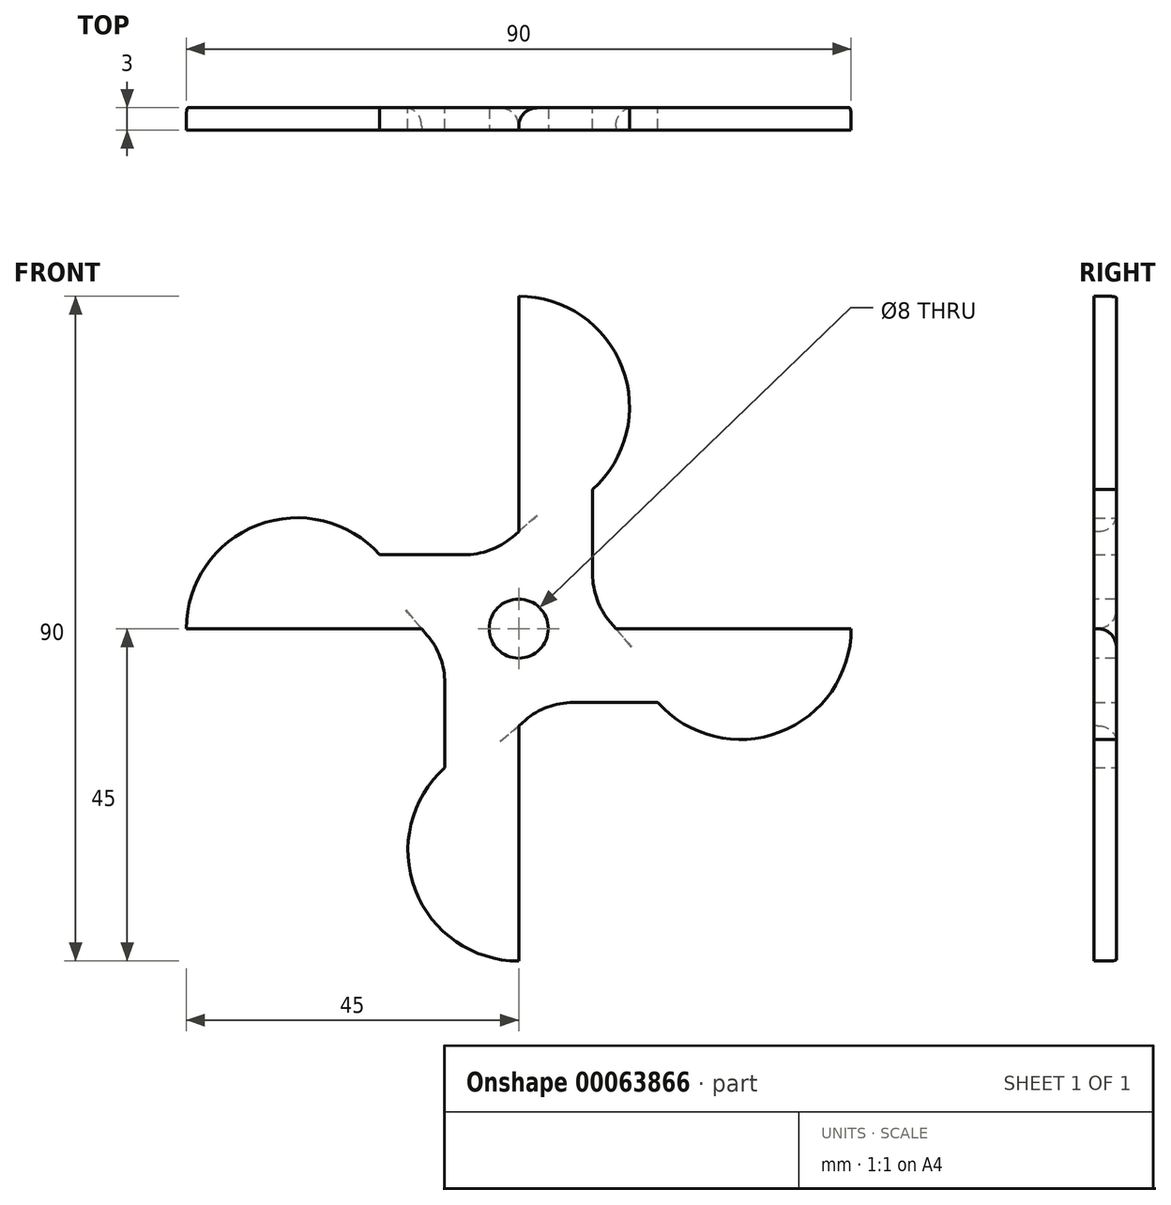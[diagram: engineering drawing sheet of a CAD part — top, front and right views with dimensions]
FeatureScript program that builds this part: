
annotation { "Feature Type Name" : "Feature", "Feature Type Description" : "" }
export const myFeature = defineFeature(function(context is Context, id is Id, definition is map)
    precondition{}
    {
        {
            var Q0;
            Q0=qCreatedBy(makeId("Front.planeOp"),FACE);
            var sketch = newSketch(context, id + "F0", { "sketchPlane" : qUnion([Q0])});
            skArc(sketch, "E0", {"start": v(10, 18.82) * mm, "mid": v(14.01, 35.35) * mm, "end": v(0, 45) * mm});
            skArc(sketch, "E1", {"start": v(10, 21.7) * mm, "mid": v(11.77, 35.52) * mm, "end": v(0, 43) * mm});
            skLineSegment(sketch, "E2", {"start": v(0, 13.15) * mm, "end": v(0, 10) * mm});
            skLineSegment(sketch, "E3", {"start": v(10, 7.38) * mm, "end": v(10, 18.82) * mm});
            skLineSegment(sketch, "E4", {"start": v(0, 43) * mm, "end": v(0, 45) * mm});
            skArc(sketch, "E5.1.1", {"start": v(-21.7, 10) * mm, "mid": v(-35.52, 11.77) * mm, "end": v(-43, 0) * mm});
            skLineSegment(sketch, "E5.1.2", {"start": v(-43, 0) * mm, "end": v(-45, 0) * mm});
            skArc(sketch, "E5.1.3", {"start": v(-18.82, 10) * mm, "mid": v(-35.35, 14.01) * mm, "end": v(-45, 0) * mm});
            skLineSegment(sketch, "E5.1.4", {"start": v(-7.38, 10) * mm, "end": v(-18.82, 10) * mm});
            skArc(sketch, "E5.2.1", {"start": v(-10, -21.7) * mm, "mid": v(-11.77, -35.52) * mm, "end": v(0, -43) * mm});
            skLineSegment(sketch, "E5.2.2", {"start": v(0, -43) * mm, "end": v(0, -45) * mm});
            skArc(sketch, "E5.2.3", {"start": v(-10, -18.82) * mm, "mid": v(-14.01, -35.35) * mm, "end": v(0, -45) * mm});
            skLineSegment(sketch, "E5.2.4", {"start": v(-10, -7.38) * mm, "end": v(-10, -18.82) * mm});
            skLineSegment(sketch, "E5.3.0", {"start": v(17, 0) * mm, "end": v(17, 0) * mm});
            skArc(sketch, "E5.3.1", {"start": v(21.7, -10) * mm, "mid": v(35.52, -11.77) * mm, "end": v(43, 0) * mm});
            skLineSegment(sketch, "E5.3.2", {"start": v(43, 0) * mm, "end": v(45, 0) * mm});
            skArc(sketch, "E5.3.3", {"start": v(18.82, -10) * mm, "mid": v(35.35, -14.01) * mm, "end": v(45, 0) * mm});
            skLineSegment(sketch, "E5.3.4", {"start": v(7.38, -10) * mm, "end": v(18.82, -10) * mm});
            skPoint(sketch, "E5.center", {"position": v(0, 0) * mm});
            skPoint(sketch, "E6.visualSharp", {"position": v(10, 0) * mm});
            skLineSegment(sketch, "E7", {"start": v(10, 21.7) * mm, "end": v(-0.88, 12.4) * mm});
            skPoint(sketch, "E8.orphan", {"position": v(0, 17) * mm});
            skPoint(sketch, "E9.newPointB", {"position": v(0, 10) * mm});
            skArc(sketch, "E9.filletArc", {"start": v(-7.38, 10) * mm, "mid": v(-3.92, 10.62) * mm, "end": v(-0.88, 12.4) * mm});
            skArc(sketch, "E10.1.0", {"start": v(-10, -7.38) * mm, "mid": v(-10.62, -3.92) * mm, "end": v(-12.4, -0.88) * mm});
            skLineSegment(sketch, "E10.1.1", {"start": v(-21.7, 10) * mm, "end": v(-12.4, -0.88) * mm});
            skArc(sketch, "E10.2.0", {"start": v(7.38, -10) * mm, "mid": v(3.92, -10.62) * mm, "end": v(0.88, -12.4) * mm});
            skLineSegment(sketch, "E10.2.1", {"start": v(-10, -21.7) * mm, "end": v(0.88, -12.4) * mm});
            skArc(sketch, "E10.3.0", {"start": v(10, 7.38) * mm, "mid": v(10.62, 3.92) * mm, "end": v(12.4, 0.88) * mm});
            skLineSegment(sketch, "E10.3.1", {"start": v(21.7, -10) * mm, "end": v(12.4, 0.88) * mm});
            skPoint(sketch, "E11.orphan", {"position": v(17, 0) * mm});
            skPoint(sketch, "E12.orphan", {"position": v(10, 7) * mm});
            skPoint(sketch, "E13.orphan", {"position": v(0, -17) * mm});
            skPoint(sketch, "E14.orphan", {"position": v(0, -10) * mm});
            skPoint(sketch, "E15.orphan", {"position": v(-10, 0) * mm});
            skPoint(sketch, "E16.orphan", {"position": v(-17, 0) * mm});
            skCircle(sketch, "E17", {"center": v(0, 0) * mm, "radius": 3.75 * mm});
            skSolve(sketch);
        }
        {
            var Q0;
            Q0=makeQuery(id+"F0.imprint","IMPRINT",FACE,{"disambiguationData":[TD([[makeQuery(id+"F0.imprint","IMPRINT",EDGE,{"derivedFrom":sQuery(id+"F0.wireOp",EDGE,"E0")}),1.0]])]});
            extrude(context, id + "F1", {"entities" : qUnion([Q0]), "depth" : 5 * mm});
        }
        {
            var Q0;
            Q0=makeQuery(id+"F1.opExtrude","CAP_FACE",FACE,{"disambiguationData":[OSD([sQuery(id+"F0.wireOp",EDGE,"E0"),sQuery(id+"F0.wireOp",EDGE,"E1"),sQuery(id+"F0.wireOp",EDGE,"E3"),sQuery(id+"F0.wireOp",EDGE,"E4"),sQuery(id+"F0.wireOp",EDGE,"E5.1.1"),sQuery(id+"F0.wireOp",EDGE,"E5.1.2"),sQuery(id+"F0.wireOp",EDGE,"E5.1.3"),sQuery(id+"F0.wireOp",EDGE,"E5.1.4"),sQuery(id+"F0.wireOp",EDGE,"E5.2.1"),sQuery(id+"F0.wireOp",EDGE,"E5.2.2"),sQuery(id+"F0.wireOp",EDGE,"E5.2.3"),sQuery(id+"F0.wireOp",EDGE,"E5.2.4"),sQuery(id+"F0.wireOp",EDGE,"E5.3.1"),sQuery(id+"F0.wireOp",EDGE,"E5.3.2"),sQuery(id+"F0.wireOp",EDGE,"E5.3.3"),sQuery(id+"F0.wireOp",EDGE,"E5.3.4"),sQuery(id+"F0.wireOp",EDGE,"E7"),sQuery(id+"F0.wireOp",EDGE,"E9.filletArc"),sQuery(id+"F0.wireOp",EDGE,"E10.1.0"),sQuery(id+"F0.wireOp",EDGE,"E10.1.1"),sQuery(id+"F0.wireOp",EDGE,"E10.2.0"),sQuery(id+"F0.wireOp",EDGE,"E10.2.1"),sQuery(id+"F0.wireOp",EDGE,"E10.3.0"),sQuery(id+"F0.wireOp",EDGE,"E10.3.1"),sQuery(id+"F0.wireOp",EDGE,"E17")])],"isStart":true});
            var sketch = newSketch(context, id + "F2", { "sketchPlane" : qUnion([Q0])});
            skArc(sketch, "E18", {"start": v(0, 45) * mm, "mid": v(-14.01, 35.35) * mm, "end": v(-10, 18.82) * mm});
            skPoint(sketch, "E18.first.point", {"position": v(-2.98, 44.7) * mm});
            skPoint(sketch, "E18.second.point", {"position": v(-12.28, 38.61) * mm});
            skPoint(sketch, "E18.third.point", {"position": v(-10.97, 19.77) * mm});
            skLineSegment(sketch, "E19", {"start": v(0, 9.88) * mm, "end": v(0, 45) * mm});
            skLineSegment(sketch, "E20", {"start": v(-10, 18.82) * mm, "end": v(-10, 7.38) * mm});
            skArc(sketch, "E21", {"start": v(-12.4, 0.88) * mm, "mid": v(-10.62, 3.92) * mm, "end": v(-10, 7.38) * mm});
            skPoint(sketch, "E21.first.point", {"position": v(-11.49, 2.13) * mm});
            skPoint(sketch, "E21.second.point", {"position": v(-11, 3.02) * mm});
            skPoint(sketch, "E21.third.point", {"position": v(-10.2, 5.4) * mm});
            skLineSegment(sketch, "E22", {"start": v(-13.15, 0) * mm, "end": v(-12.4, 0.88) * mm});
            skLineSegment(sketch, "E23", {"start": v(-13.15, 0) * mm, "end": v(-3.75, 0) * mm});
            skLineSegment(sketch, "E24", {"start": v(0, 3.75) * mm, "end": v(0, 9.88) * mm});
            skArc(sketch, "E25", {"start": v(0, 3.75) * mm, "mid": v(-2.65, 2.65) * mm, "end": v(-3.75, 0) * mm});
            skPoint(sketch, "E25.third.point", {"position": v(-2.3, 2.96) * mm});
            skArc(sketch, "E26.1.0", {"start": v(-3.75, 0) * mm, "mid": v(-2.65, -2.65) * mm, "end": v(0, -3.75) * mm});
            skLineSegment(sketch, "E26.1.1", {"start": v(0, -13.15) * mm, "end": v(-0.88, -12.4) * mm});
            skArc(sketch, "E26.1.2", {"start": v(-0.88, -12.4) * mm, "mid": v(-3.92, -10.62) * mm, "end": v(-7.38, -10) * mm});
            skLineSegment(sketch, "E26.1.3", {"start": v(-18.82, -10) * mm, "end": v(-7.38, -10) * mm});
            skArc(sketch, "E26.1.4", {"start": v(-45, 0) * mm, "mid": v(-35.35, -14.01) * mm, "end": v(-18.82, -10) * mm});
            skLineSegment(sketch, "E26.1.5", {"start": v(-9.88, 0) * mm, "end": v(-45, 0) * mm});
            skLineSegment(sketch, "E26.1.6", {"start": v(-3.75, 0) * mm, "end": v(-9.88, 0) * mm});
            skArc(sketch, "E26.2.0", {"start": v(0, -3.75) * mm, "mid": v(2.65, -2.65) * mm, "end": v(3.75, 0) * mm});
            skLineSegment(sketch, "E26.2.1", {"start": v(13.15, 0) * mm, "end": v(12.4, -0.88) * mm});
            skArc(sketch, "E26.2.2", {"start": v(12.4, -0.88) * mm, "mid": v(10.62, -3.92) * mm, "end": v(10, -7.38) * mm});
            skLineSegment(sketch, "E26.2.3", {"start": v(10, -18.82) * mm, "end": v(10, -7.38) * mm});
            skArc(sketch, "E26.2.4", {"start": v(0, -45) * mm, "mid": v(14.01, -35.35) * mm, "end": v(10, -18.82) * mm});
            skLineSegment(sketch, "E26.2.5", {"start": v(0, -9.88) * mm, "end": v(0, -45) * mm});
            skLineSegment(sketch, "E26.2.6", {"start": v(0, -3.75) * mm, "end": v(0, -9.88) * mm});
            skArc(sketch, "E26.3.0", {"start": v(3.75, 0) * mm, "mid": v(2.65, 2.65) * mm, "end": v(0, 3.75) * mm});
            skLineSegment(sketch, "E26.3.1", {"start": v(0, 13.15) * mm, "end": v(0.88, 12.4) * mm});
            skArc(sketch, "E26.3.2", {"start": v(0.88, 12.4) * mm, "mid": v(3.92, 10.62) * mm, "end": v(7.38, 10) * mm});
            skLineSegment(sketch, "E26.3.3", {"start": v(18.82, 10) * mm, "end": v(7.38, 10) * mm});
            skArc(sketch, "E26.3.4", {"start": v(45, 0) * mm, "mid": v(35.35, 14.01) * mm, "end": v(18.82, 10) * mm});
            skLineSegment(sketch, "E26.3.5", {"start": v(9.88, 0) * mm, "end": v(45, 0) * mm});
            skLineSegment(sketch, "E26.3.6", {"start": v(3.75, 0) * mm, "end": v(9.88, 0) * mm});
            skSolve(sketch);
        }
        {
            var Q0;
            {var subQ1=makeQuery(id+"F1.opExtrude","CAP_EDGE",EDGE,{"disambiguationData":[OSD([sQuery(id+"F0.wireOp",EDGE,"E1")])],"isStart":true});Q0=makeQuery(id+"F2.imprint","IMPRINT",FACE,{"disambiguationData":[TD([[makeQuery(id+"F2.imprint","IMPRINT",EDGE,{"derivedFrom":subQ1}),-1.0]])]});}
            var Q1;
            {var subQ6=sQuery(id+"F2.wireOp",EDGE,"E18");Q1=makeQuery(id+"F2.imprint","IMPRINT",FACE,{"disambiguationData":[TD([[makeQuery(id+"F2.imprint","IMPRINT",EDGE,{"derivedFrom":subQ6}),-1.0]])]});}
            var Q2;
            {var subQ4=sQuery(id+"F2.wireOp",EDGE,"E24");Q2=makeQuery(id+"F2.imprint","IMPRINT",FACE,{"disambiguationData":[TD([[makeQuery(id+"F2.imprint","IMPRINT",EDGE,{"derivedFrom":subQ4}),-1.0]])]});}
            var Q3;
            {var subQ1=makeQuery(id+"F1.opExtrude","CAP_EDGE",EDGE,{"disambiguationData":[OSD([sQuery(id+"F0.wireOp",EDGE,"E5.1.1")])],"isStart":true});Q3=makeQuery(id+"F2.imprint","IMPRINT",FACE,{"disambiguationData":[TD([[makeQuery(id+"F2.imprint","IMPRINT",EDGE,{"derivedFrom":subQ1}),-1.0]])]});}
            var Q4;
            Q4=makeQuery(id+"F2.imprint","IMPRINT",FACE,{"disambiguationData":[TD([[makeQuery(id+"F2.imprint","IMPRINT",EDGE,{"derivedFrom":sQuery(id+"F2.wireOp",EDGE,"E26.2.0")}),1.0]])]});
            var Q5;
            {var subQ1=makeQuery(id+"F1.opExtrude","CAP_EDGE",EDGE,{"disambiguationData":[OSD([sQuery(id+"F0.wireOp",EDGE,"E5.2.1")])],"isStart":true});Q5=makeQuery(id+"F2.imprint","IMPRINT",FACE,{"disambiguationData":[TD([[makeQuery(id+"F2.imprint","IMPRINT",EDGE,{"derivedFrom":subQ1}),-1.0]])]});}
            var Q6;
            Q6=makeQuery(id+"F2.imprint","IMPRINT",FACE,{"disambiguationData":[TD([[makeQuery(id+"F2.imprint","IMPRINT",EDGE,{"derivedFrom":sQuery(id+"F2.wireOp",EDGE,"E26.1.0")}),1.0]])]});
            var Q7;
            {var subQ1=makeQuery(id+"F1.opExtrude","CAP_EDGE",EDGE,{"disambiguationData":[OSD([sQuery(id+"F0.wireOp",EDGE,"E5.3.1")])],"isStart":true});Q7=makeQuery(id+"F2.imprint","IMPRINT",FACE,{"disambiguationData":[TD([[makeQuery(id+"F2.imprint","IMPRINT",EDGE,{"derivedFrom":subQ1}),-1.0]])]});}
            extrude(context, id + "F3", {"entities" : qUnion([Q0, Q1, Q2, Q3, Q4, Q5, Q6, Q7]), "operationType" : NewBodyOperationType.ADD, "depth" : 3 * mm});
        }
        {
            var Q0;
            Q0=makeQuery(id+"F1.opExtrude","CAP_FACE",FACE,{"disambiguationData":[OSD([sQuery(id+"F0.wireOp",EDGE,"E0"),sQuery(id+"F0.wireOp",EDGE,"E1"),sQuery(id+"F0.wireOp",EDGE,"E3"),sQuery(id+"F0.wireOp",EDGE,"E4"),sQuery(id+"F0.wireOp",EDGE,"E5.1.1"),sQuery(id+"F0.wireOp",EDGE,"E5.1.2"),sQuery(id+"F0.wireOp",EDGE,"E5.1.3"),sQuery(id+"F0.wireOp",EDGE,"E5.1.4"),sQuery(id+"F0.wireOp",EDGE,"E5.2.1"),sQuery(id+"F0.wireOp",EDGE,"E5.2.2"),sQuery(id+"F0.wireOp",EDGE,"E5.2.3"),sQuery(id+"F0.wireOp",EDGE,"E5.2.4"),sQuery(id+"F0.wireOp",EDGE,"E5.3.1"),sQuery(id+"F0.wireOp",EDGE,"E5.3.2"),sQuery(id+"F0.wireOp",EDGE,"E5.3.3"),sQuery(id+"F0.wireOp",EDGE,"E5.3.4"),sQuery(id+"F0.wireOp",EDGE,"E7"),sQuery(id+"F0.wireOp",EDGE,"E9.filletArc"),sQuery(id+"F0.wireOp",EDGE,"E10.1.0"),sQuery(id+"F0.wireOp",EDGE,"E10.1.1"),sQuery(id+"F0.wireOp",EDGE,"E10.2.0"),sQuery(id+"F0.wireOp",EDGE,"E10.2.1"),sQuery(id+"F0.wireOp",EDGE,"E10.3.0"),sQuery(id+"F0.wireOp",EDGE,"E10.3.1"),sQuery(id+"F0.wireOp",EDGE,"E17")])],"isStart":false});
            var sketch = newSketch(context, id + "F4", { "sketchPlane" : qUnion([Q0])});
            skCircle(sketch, "E27", {"center": v(0, 0) * mm, "radius": 55.53 * mm});
            skSolve(sketch);
        }
        {
            var Q0;
            Q0 = qSketchRegion(id + "F4", true);
            extrude(context, id + "F5", {"entities" : qUnion([Q0]), "operationType" : NewBodyOperationType.REMOVE, "oppositeDirection" : true, "depth" : 5 * mm});
        }
        {
            var Q0;
            Q0=makeQuery(id+"F3.opExtrude","CAP_EDGE",EDGE,{"disambiguationData":[OSD([sQuery(id+"F2.wireOp",EDGE,"E26.1.5")])],"isStart":false});
            var Q1;
            Q1=makeQuery(id+"F3.opExtrude","CAP_EDGE",EDGE,{"disambiguationData":[OSD([sQuery(id+"F2.wireOp",EDGE,"E19")])],"isStart":false});
            var Q2;
            Q2=makeQuery(id+"F3.opExtrude","CAP_EDGE",EDGE,{"disambiguationData":[OSD([sQuery(id+"F2.wireOp",EDGE,"E26.3.5")])],"isStart":false});
            var Q3;
            Q3=makeQuery(id+"F3.opExtrude","CAP_EDGE",EDGE,{"disambiguationData":[OSD([sQuery(id+"F2.wireOp",EDGE,"E26.2.5")])],"isStart":false});
            fillet(context, id + "F6", {"entities" : qUnion([Q0, Q1, Q2, Q3]), "radius" : 2.5 * mm, "tangentPropagation" : true, "allowEdgeOverflow" : false});
        }
        {
            var Q0;
            {var subQ0=sQuery(id+"F2.wireOp",EDGE,"E22");var subQ1=sQuery(id+"F2.wireOp",EDGE,"E26.1.5");var subQ2=sQuery(id+"F2.wireOp",EDGE,"E26.3.5");var subQ3=sQuery(id+"F2.wireOp",EDGE,"E26.3.1");var subQ4=sQuery(id+"F2.wireOp",EDGE,"E26.2.5");var subQ5=sQuery(id+"F2.wireOp",EDGE,"E26.2.1");var subQ6=sQuery(id+"F2.wireOp",EDGE,"E26.1.1");var subQ7=sQuery(id+"F2.wireOp",EDGE,"E19");var subQ8=makeQuery(id+"F3.opExtrude","CAP_FACE",FACE,{"disambiguationData":[OSD([sQuery(id+"F2.wireOp",EDGE,"E18"),subQ7,sQuery(id+"F2.wireOp",EDGE,"E20"),sQuery(id+"F2.wireOp",EDGE,"E21"),subQ0,sQuery(id+"F2.wireOp",EDGE,"E25"),sQuery(id+"F2.wireOp",EDGE,"E26.1.0"),subQ6,sQuery(id+"F2.wireOp",EDGE,"E26.1.2"),sQuery(id+"F2.wireOp",EDGE,"E26.1.3"),sQuery(id+"F2.wireOp",EDGE,"E26.1.4"),subQ1,sQuery(id+"F2.wireOp",EDGE,"E26.2.0"),subQ5,sQuery(id+"F2.wireOp",EDGE,"E26.2.2"),sQuery(id+"F2.wireOp",EDGE,"E26.2.3"),sQuery(id+"F2.wireOp",EDGE,"E26.2.4"),subQ4,sQuery(id+"F2.wireOp",EDGE,"E26.3.0"),subQ3,sQuery(id+"F2.wireOp",EDGE,"E26.3.2"),sQuery(id+"F2.wireOp",EDGE,"E26.3.3"),sQuery(id+"F2.wireOp",EDGE,"E26.3.4"),subQ2])],"isStart":true});Q0=makeQuery(id+"F5.boolean.opBoolean","MERGE",FACE,{"derivedFrom":[makeQuery(id+"F3.boolean.opBoolean","SPLIT",FACE,{"disambiguationData":[TD([makeQuery(id+"F1.opExtrude","SWEPT_FACE",FACE,{"disambiguationData":[OSD([sQuery(id+"F0.wireOp",EDGE,"E1")])]})])],"derivedFrom":subQ8}),makeQuery(id+"F3.boolean.opBoolean","SPLIT",FACE,{"disambiguationData":[TD([makeQuery(id+"F1.opExtrude","SWEPT_FACE",FACE,{"disambiguationData":[OSD([sQuery(id+"F0.wireOp",EDGE,"E5.1.1")])]})])],"derivedFrom":subQ8}),makeQuery(id+"F3.boolean.opBoolean","SPLIT",FACE,{"disambiguationData":[TD([makeQuery(id+"F1.opExtrude","SWEPT_FACE",FACE,{"disambiguationData":[OSD([sQuery(id+"F0.wireOp",EDGE,"E5.2.1")])]})])],"derivedFrom":subQ8}),makeQuery(id+"F3.boolean.opBoolean","SPLIT",FACE,{"disambiguationData":[TD([makeQuery(id+"F1.opExtrude","SWEPT_FACE",FACE,{"disambiguationData":[OSD([sQuery(id+"F0.wireOp",EDGE,"E5.3.1")])]})])],"derivedFrom":subQ8}),makeQuery(id+"F5.opExtrude","CAP_FACE",FACE,{"disambiguationData":[OSD([sQuery(id+"F4.wireOp",EDGE,"E27")])],"isStart":false})]});}
            var sketch = newSketch(context, id + "F7", { "sketchPlane" : qUnion([Q0])});
            skCircle(sketch, "E28", {"center": v(0, 0) * mm, "radius": 4 * mm});
            skSolve(sketch);
        }
        {
            var Q0;
            Q0 = qSketchRegion(id + "F7", true);
            extrude(context, id + "F8", {"entities" : qUnion([Q0]), "operationType" : NewBodyOperationType.REMOVE, "endBound" : BoundingType.THROUGH_ALL, "oppositeDirection" : true, "depth" : 25 * mm});
        }
    });
